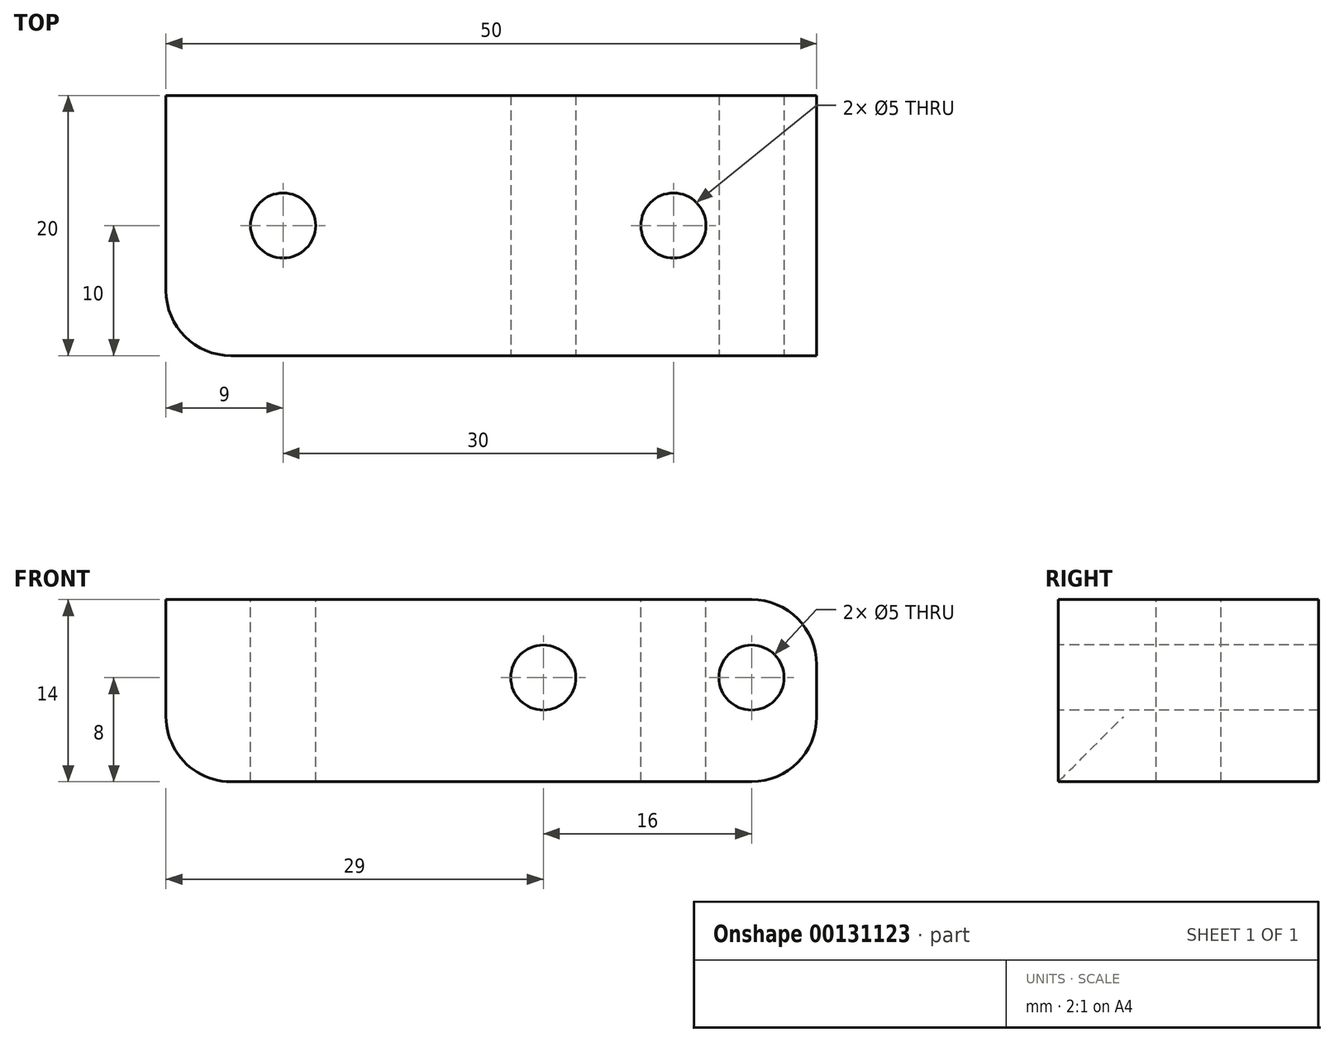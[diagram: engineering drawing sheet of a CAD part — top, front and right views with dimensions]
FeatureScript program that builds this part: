
annotation { "Feature Type Name" : "Feature", "Feature Type Description" : "" }
export const myFeature = defineFeature(function(context is Context, id is Id, definition is map)
    precondition{}
    {
        {
            var Q0;
            Q0=qCreatedBy(makeId("Right.planeOp"),FACE);
            var sketch = newSketch(context, id + "F0", { "sketchPlane" : qUnion([Q0])});
            skLineSegment(sketch, "E0.bottom", {"start": v(10, -7) * mm, "end": v(-10, -7) * mm});
            skLineSegment(sketch, "E0.top", {"start": v(10, 7) * mm, "end": v(-10, 7) * mm});
            skLineSegment(sketch, "E0.left", {"start": v(10, -7) * mm, "end": v(10, 7) * mm});
            skLineSegment(sketch, "E0.right", {"start": v(-10, -7) * mm, "end": v(-10, 7) * mm});
            skPoint(sketch, "E0.middle", {"position": v(0, 0) * mm});
            skSolve(sketch);
        }
        {
            var Q0;
            Q0=makeQuery(id+"F0.imprint","IMPRINT",FACE,{"disambiguationData":[TD([[makeQuery(id+"F0.imprint","IMPRINT",EDGE,{"derivedFrom":sQuery(id+"F0.wireOp",EDGE,"E0.bottom")}),-1.0]])]});
            extrude(context, id + "F1", {"entities" : qUnion([Q0]), "endBound" : BoundingType.SYMMETRIC, "depth" : 50 * mm});
        }
        {
            var Q0;
            Q0=makeQuery(id+"F1.opExtrude","SWEPT_FACE",FACE,{"disambiguationData":[OSD([sQuery(id+"F0.wireOp",EDGE,"E0.right")])]});
            var sketch = newSketch(context, id + "F2", { "sketchPlane" : qUnion([Q0])});
            skPoint(sketch, "E1", {"position": v(4, 1) * mm});
            skPoint(sketch, "E2", {"position": v(20, 1) * mm});
            skSolve(sketch);
        }
        {
            var Q0;
            Q0=sQuery(id+"F2.wireOp",VERTEX,"E1");
            var Q1;
            Q1=sQuery(id+"F2.wireOp",VERTEX,"E2");
            var Q2;
            Q2=makeQuery(id+"F1.opExtrude","SWEPT_BODY",BODY,{"disambiguationData":[OSD([sQuery(id+"F0.wireOp",EDGE,"E0.bottom"),sQuery(id+"F0.wireOp",EDGE,"E0.top"),sQuery(id+"F0.wireOp",EDGE,"E0.left"),sQuery(id+"F0.wireOp",EDGE,"E0.right")])]});
            hole(context, id + "F3", {"style" : HoleStyle.SIMPLE, "endStyle" : HoleEndStyle.THROUGH, "standardTappedOrClearance" : lookupTablePath({ "standard" : "Custom", "fit" : "Normal", "size" : "M6", "type" : "Clearance" }), "standardBlindInLast" : lookupTablePath({ "fit" : "Standard", "standard" : "Custom", "size" : "M6", "type" : "Clearance" }), "holeDiameter" : 5 * mm, "locations" : qUnion([Q0, Q1]), "scope" : qUnion([Q2]), "isTappedThrough" : true});
        }
        {
            var Q0;
            Q0=makeQuery(id+"F1.opExtrude","SWEPT_FACE",FACE,{"disambiguationData":[OSD([sQuery(id+"F0.wireOp",EDGE,"E0.top")])]});
            var sketch = newSketch(context, id + "F4", { "sketchPlane" : qUnion([Q0])});
            skPoint(sketch, "E3", {"position": v(-16, 0) * mm});
            skPoint(sketch, "E3.positionSnap0", {"position": v(-25, 0) * mm});
            skPoint(sketch, "E4", {"position": v(14, 0) * mm});
            skSolve(sketch);
        }
        {
            var Q0;
            Q0=sQuery(id+"F4.wireOp",VERTEX,"E3");
            var Q1;
            Q1=sQuery(id+"F4.wireOp",VERTEX,"E4");
            var Q2;
            Q2=makeQuery(id+"F1.opExtrude","SWEPT_BODY",BODY,{"disambiguationData":[OSD([sQuery(id+"F0.wireOp",EDGE,"E0.bottom"),sQuery(id+"F0.wireOp",EDGE,"E0.top"),sQuery(id+"F0.wireOp",EDGE,"E0.left"),sQuery(id+"F0.wireOp",EDGE,"E0.right")])]});
            hole(context, id + "F5", {"style" : HoleStyle.SIMPLE, "endStyle" : HoleEndStyle.THROUGH, "holeDiameter" : 5 * mm, "locations" : qUnion([Q0, Q1]), "scope" : qUnion([Q2]), "isTappedThrough" : true});
        }
        {
            var Q0;
            Q0=makeQuery(id+"F1.opExtrude","CAP_EDGE",EDGE,{"disambiguationData":[OSD([sQuery(id+"F0.wireOp",EDGE,"E0.top")])],"isStart":false});
            var Q1;
            Q1=makeQuery(id+"F1.opExtrude","CAP_EDGE",EDGE,{"disambiguationData":[OSD([sQuery(id+"F0.wireOp",EDGE,"E0.bottom")])],"isStart":true});
            var Q2;
            Q2=makeQuery(id+"F1.opExtrude","CAP_EDGE",EDGE,{"disambiguationData":[OSD([sQuery(id+"F0.wireOp",EDGE,"E0.bottom")])],"isStart":false});
            fillet(context, id + "F6", {"entities" : qUnion([Q0, Q1, Q2]), "radius" : 5 * mm, "tangentPropagation" : true, "allowEdgeOverflow" : false});
        }
        {
            var Q0;
            Q0=makeQuery(id+"F1.opExtrude","CAP_EDGE",EDGE,{"disambiguationData":[OSD([sQuery(id+"F0.wireOp",EDGE,"E0.right")])],"isStart":true});
            fillet(context, id + "F7", {"entities" : qUnion([Q0]), "radius" : 5 * mm, "allowEdgeOverflow" : false});
        }
    });
